# Revit family: Illuminated Display Solution
name_source: partatom
category: Generic Models
revit_build: Autodesk Revit 2014 (Build: 20130308_1515(x64)
units: mm (PartAtom-declared; Revit-internal decimal feet)

## types (1)
- Illuminated Display Solution
    Model = Vesta Illuminated Display Solution
    UFBD - Depth = 1' - 6"
    UFBD - Height = 0' - 6"
    UFDPUSEF - End Panel Base Height = 0' - 6"
    UFDPUSEF - End Panel Height = 6' - 0"
    UFDPUSEF - End Panel Width = 3' - 0"
    UFDT - Base Height = 0' - 6"
    UFDT - Depth = 1' - 4"
    UFDT - Height = 1' - 0"
    UFGC - Center Panel Base Height = 0' - 6"
    UFGC - Center Panel Height = 6' - 0"
    UFGC - Center Panel Width = 3' - 0"
    UFUSA - Ends - Depth = 1' - 6"
    UFUSA - Left - Depth = 1' - 6"
    UFUSA - Right - Depth = 1' - 6"
    UFWDPU - Base Panel Height = 0' - 6"
    UFWDPU - End Panel Height = 6' - 0"
    UFWDPU - Panel Width = 1' - 6"
    URL = http://madixinc.com

## geometry (parser evidence)
native form markers: Sweep x15
no freeform markers — native parametric forms only
